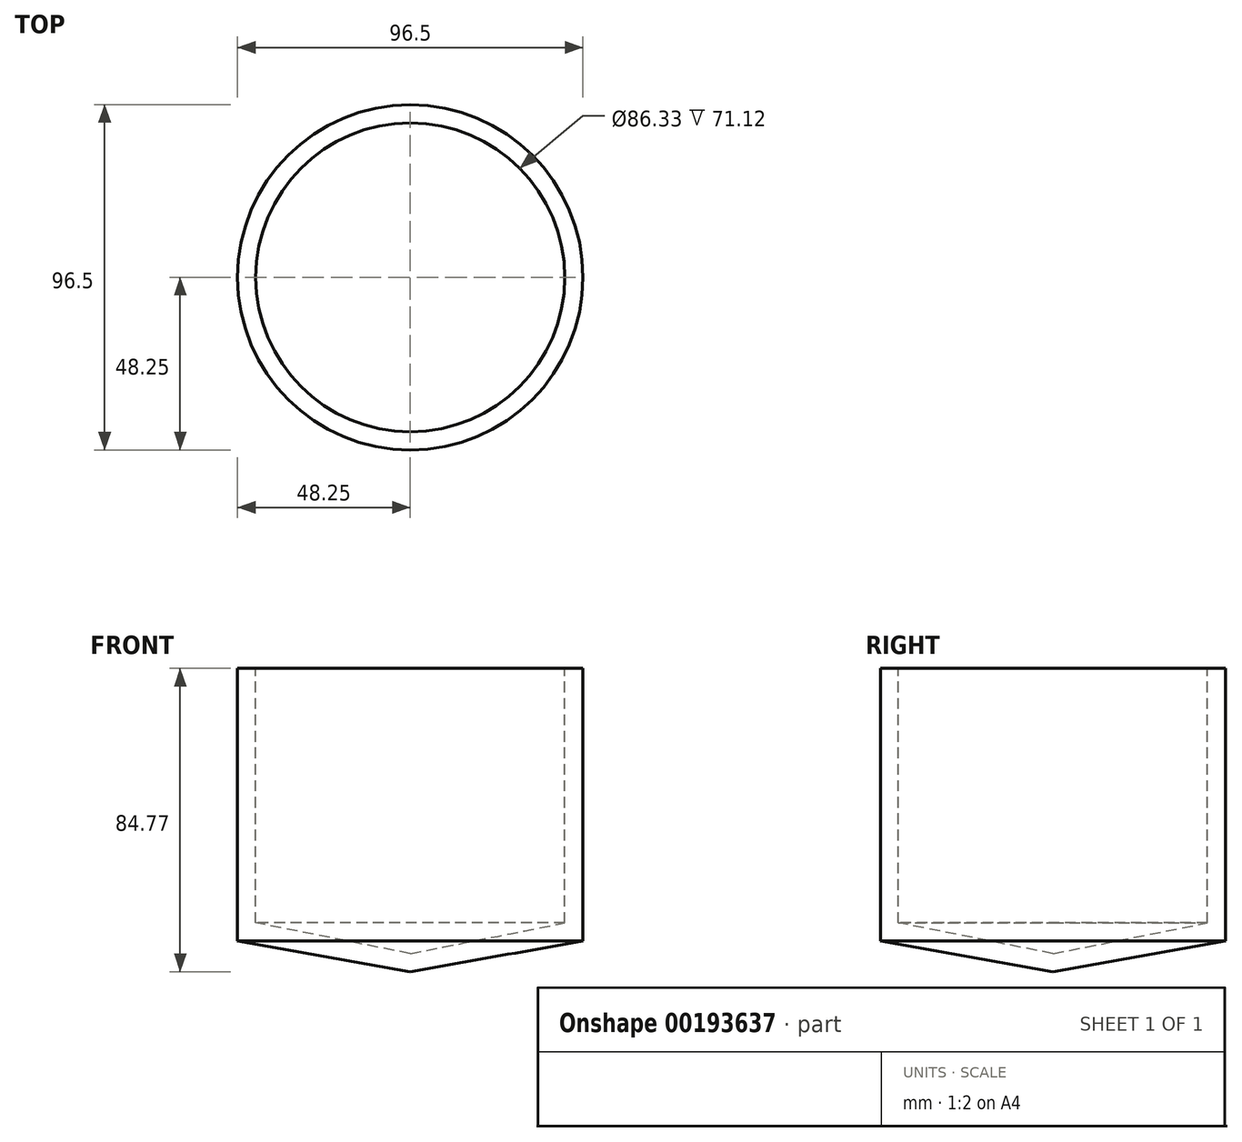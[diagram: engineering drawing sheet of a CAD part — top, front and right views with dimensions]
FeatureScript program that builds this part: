
annotation { "Feature Type Name" : "Feature", "Feature Type Description" : "" }
export const myFeature = defineFeature(function(context is Context, id is Id, definition is map)
    precondition{}
    {
        {
            var Q0;
            Q0=qCreatedBy(makeId("Front.planeOp"),FACE);
            var sketch = newSketch(context, id + "F0", { "sketchPlane" : qUnion([Q0])});
            skLineSegment(sketch, "E0", {"start": v(0, 43.26) * mm, "end": v(0, -41.51) * mm});
            skLineSegment(sketch, "E1", {"start": v(43.17, 43.26) * mm, "end": v(43.17, -27.86) * mm});
            skLineSegment(sketch, "E2", {"start": v(43.17, -27.86) * mm, "end": v(0, -36.45) * mm});
            skLineSegment(sketch, "E3", {"start": v(0, -41.51) * mm, "end": v(48.25, -32.94) * mm});
            skLineSegment(sketch, "E4", {"start": v(48.25, -32.94) * mm, "end": v(48.25, 43.26) * mm});
            skLineSegment(sketch, "E5", {"start": v(48.25, 43.26) * mm, "end": v(43.17, 43.26) * mm});
            skSolve(sketch);
        }
        {
            var Q0;
            Q0=makeQuery(id+"F0.imprint","IMPRINT",FACE,{"disambiguationData":[TD([[makeQuery(id+"F0.imprint","IMPRINT",EDGE,{"derivedFrom":sQuery(id+"F0.wireOp",EDGE,"E1")}),1.0]])]});
            var Q1;
            Q1=sQuery(id+"F0.wireOp",EDGE,"E0");
            revolve(context, id + "F1", {"entities" : qUnion([Q0]), "axis" : qUnion([Q1]), "revolveType" : RevolveType.FULL});
        }
    });
